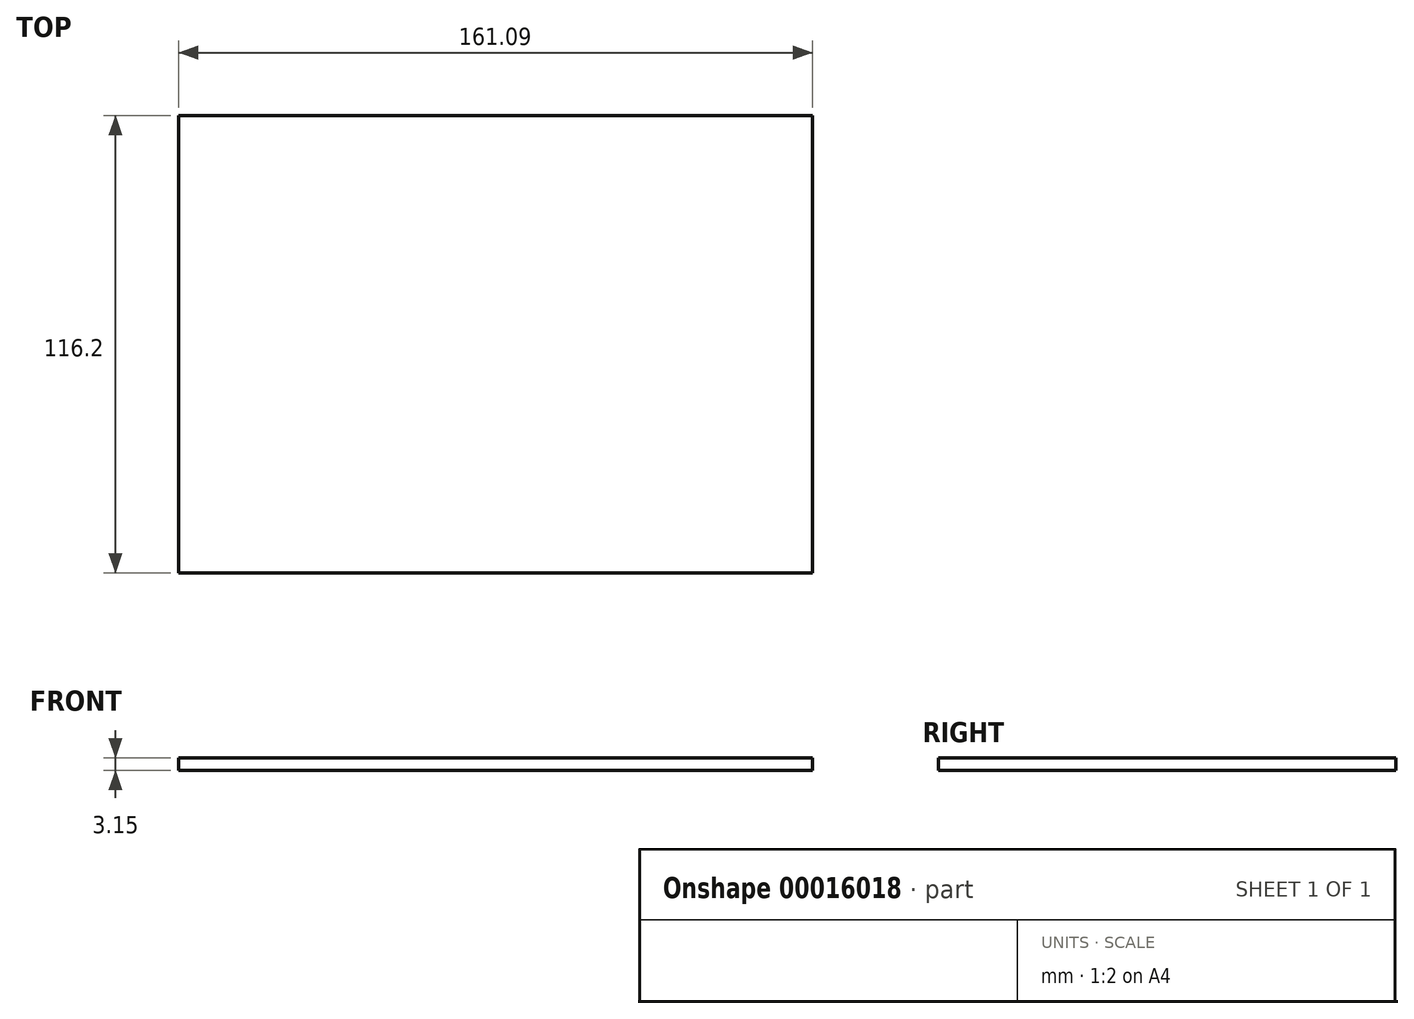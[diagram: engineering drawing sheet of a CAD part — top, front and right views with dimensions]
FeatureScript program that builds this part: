
annotation { "Feature Type Name" : "Feature", "Feature Type Description" : "" }
export const myFeature = defineFeature(function(context is Context, id is Id, definition is map)
    precondition{}
    {
        {
            var Q0;
            Q0=qCreatedBy(makeId("Top.planeOp"),FACE);
            var sketch = newSketch(context, id + "F0", { "sketchPlane" : qUnion([Q0])});
            skLineSegment(sketch, "E0.bottom", {"start": v(-54.23, 76.27) * mm, "end": v(106.86, 76.27) * mm});
            skLineSegment(sketch, "E0.top", {"start": v(-54.23, -39.93) * mm, "end": v(106.86, -39.93) * mm});
            skLineSegment(sketch, "E0.left", {"start": v(-54.23, 76.27) * mm, "end": v(-54.23, -39.93) * mm});
            skLineSegment(sketch, "E0.right", {"start": v(106.86, 76.27) * mm, "end": v(106.86, -39.93) * mm});
            skSolve(sketch);
        }
        {
            var Q0;
            Q0=makeQuery(id+"F0.imprint","IMPRINT",FACE,{"disambiguationData":[TD([[makeQuery(id+"F0.imprint","IMPRINT",EDGE,{"derivedFrom":sQuery(id+"F0.wireOp",EDGE,"E0.bottom")}),-1.0]])]});
            extrude(context, id + "F1", {"entities" : qUnion([Q0]), "depth" : 3.15 * mm});
        }
    });
